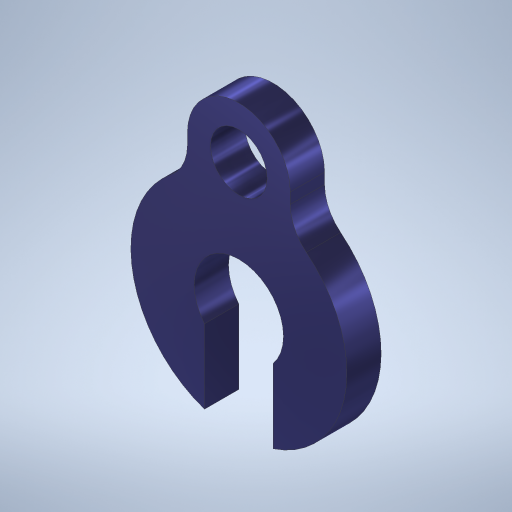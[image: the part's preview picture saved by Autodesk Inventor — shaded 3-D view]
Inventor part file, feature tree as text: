
AUTODESK INVENTOR PART (.ipt)
format: ipt  version: 2023.1 (Build 271208000, 208)  size: 286,208 bytes
history: native  units: in
note: dims shown in document units (in); Inventor stores cm internally (conversion verified against a paired STEP export)
features: extrude x1, fillet x1, sketch x1
ambient origin geometry x8: Origin, YZ Plane, XZ Plane, XY Plane, X Axis, Y Axis, Z Axis, Center Point
bodies: Solid1 (feature_tree)
feature tree (3):
  extrude  "Extrusion1"  Depth=0.0625in
  fillet  "Fillet1"  Radius=0.1875in
  sketch  "Sketch1"  dims[d0=0.13in d1=0.0825in d2=0.1875in d3=0.075in d4=0.1575in d5=0.1in d6=0.05in d7=0.0in d8=0.0625in]
